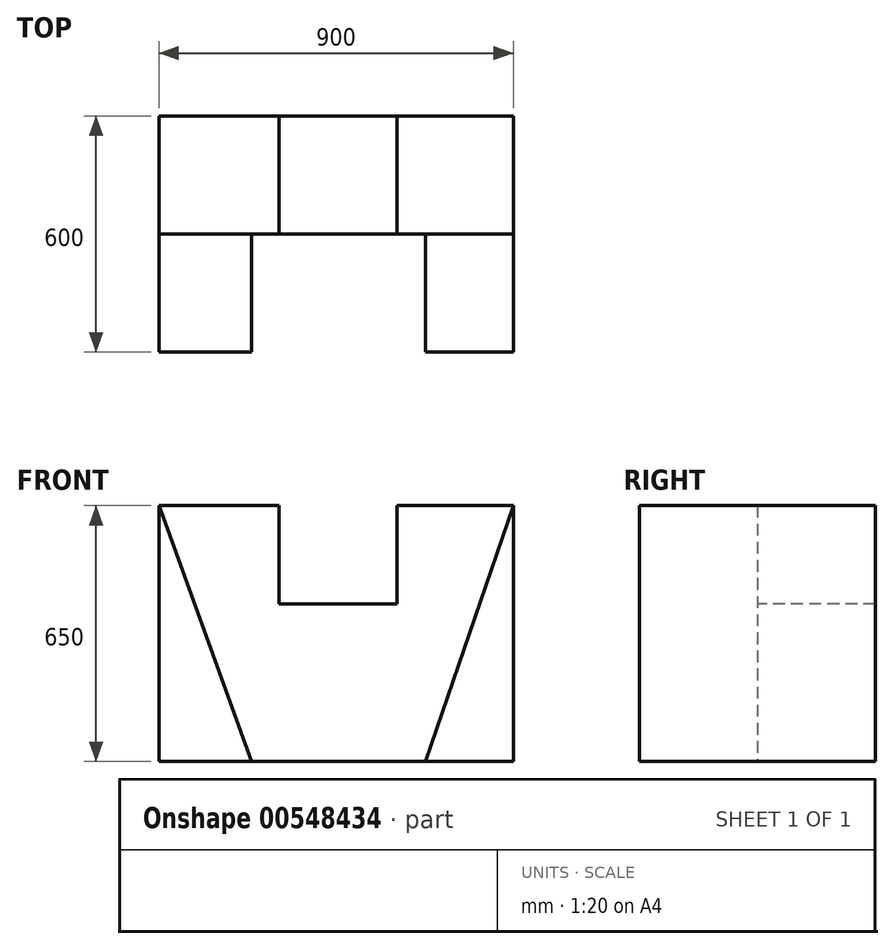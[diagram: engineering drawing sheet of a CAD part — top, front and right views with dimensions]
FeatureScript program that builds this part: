
annotation { "Feature Type Name" : "Feature", "Feature Type Description" : "" }
export const myFeature = defineFeature(function(context is Context, id is Id, definition is map)
    precondition{}
    {
        {
            var Q0;
            Q0=qCreatedBy(makeId("Front.planeOp"),FACE);
            var sketch = newSketch(context, id + "F0", { "sketchPlane" : qUnion([Q0])});
            skLineSegment(sketch, "E0.bottom", {"start": v(450, 325) * mm, "end": v(-450, 325) * mm});
            skLineSegment(sketch, "E0.top", {"start": v(450, -325) * mm, "end": v(-450, -325) * mm});
            skLineSegment(sketch, "E0.left", {"start": v(450, 325) * mm, "end": v(450, -325) * mm});
            skLineSegment(sketch, "E0.right", {"start": v(-450, 325) * mm, "end": v(-450, -325) * mm});
            skPoint(sketch, "E0.middle", {"position": v(0, 0) * mm});
            skSolve(sketch);
        }
        {
            var Q0;
            Q0 = qSketchRegion(id + "F0", true);
            extrude(context, id + "F1", {"entities" : qUnion([Q0]), "depth" : 300 * mm, "offsetDistance" : 25 * mm});
        }
        {
            var Q0;
            Q0=makeQuery(id+"F1.opExtrude","CAP_FACE",FACE,{"disambiguationData":[OSD([sQuery(id+"F0.wireOp",EDGE,"E0.bottom"),sQuery(id+"F0.wireOp",EDGE,"E0.top"),sQuery(id+"F0.wireOp",EDGE,"E0.left"),sQuery(id+"F0.wireOp",EDGE,"E0.right")])],"isStart":false});
            var sketch = newSketch(context, id + "F2", { "sketchPlane" : qUnion([Q0])});
            skLineSegment(sketch, "E1", {"start": v(450, 325) * mm, "end": v(227.1, -325) * mm});
            skLineSegment(sketch, "E2", {"start": v(-450, 325) * mm, "end": v(-214.82, -325) * mm});
            skSolve(sketch);
        }
        {
            var Q0;
            Q0 = qSketchRegion(id + "F2", true);
            var Q1;
            {var subQ0=sQuery(id+"F2.wireOp",EDGE,"E1");Q1=makeQuery(id+"F2.imprint","IMPRINT",FACE,{"disambiguationData":[TD([[makeQuery(id+"F2.imprint","IMPRINT",EDGE,{"derivedFrom":subQ0}),1.0]])]});}
            var Q2;
            {var subQ0=sQuery(id+"F2.wireOp",EDGE,"E2");Q2=makeQuery(id+"F2.imprint","IMPRINT",FACE,{"disambiguationData":[TD([[makeQuery(id+"F2.imprint","IMPRINT",EDGE,{"derivedFrom":subQ0}),-1.0]])]});}
            extrude(context, id + "F3", {"entities" : qUnion([Q0, Q1, Q2]), "operationType" : NewBodyOperationType.ADD, "depth" : 300 * mm, "offsetDistance" : 25 * mm});
        }
        {
            var Q0;
            Q0=makeQuery(id+"F1.opExtrude","CAP_FACE",FACE,{"disambiguationData":[OSD([sQuery(id+"F0.wireOp",EDGE,"E0.bottom"),sQuery(id+"F0.wireOp",EDGE,"E0.top"),sQuery(id+"F0.wireOp",EDGE,"E0.left"),sQuery(id+"F0.wireOp",EDGE,"E0.right")])],"isStart":false});
            var sketch = newSketch(context, id + "F4", { "sketchPlane" : qUnion([Q0])});
            skLineSegment(sketch, "E3.bottom", {"start": v(-144.85, 325) * mm, "end": v(155.15, 325) * mm});
            skLineSegment(sketch, "E3.top", {"start": v(-144.85, 75) * mm, "end": v(155.15, 75) * mm});
            skLineSegment(sketch, "E3.left", {"start": v(-144.85, 325) * mm, "end": v(-144.85, 75) * mm});
            skLineSegment(sketch, "E3.right", {"start": v(155.15, 325) * mm, "end": v(155.15, 75) * mm});
            skSolve(sketch);
        }
        {
            var Q0;
            Q0 = qSketchRegion(id + "F4", true);
            extrude(context, id + "F5", {"entities" : qUnion([Q0]), "operationType" : NewBodyOperationType.REMOVE, "endBound" : BoundingType.THROUGH_ALL, "oppositeDirection" : true, "depth" : 25 * mm, "offsetDistance" : 25 * mm});
        }
    });
